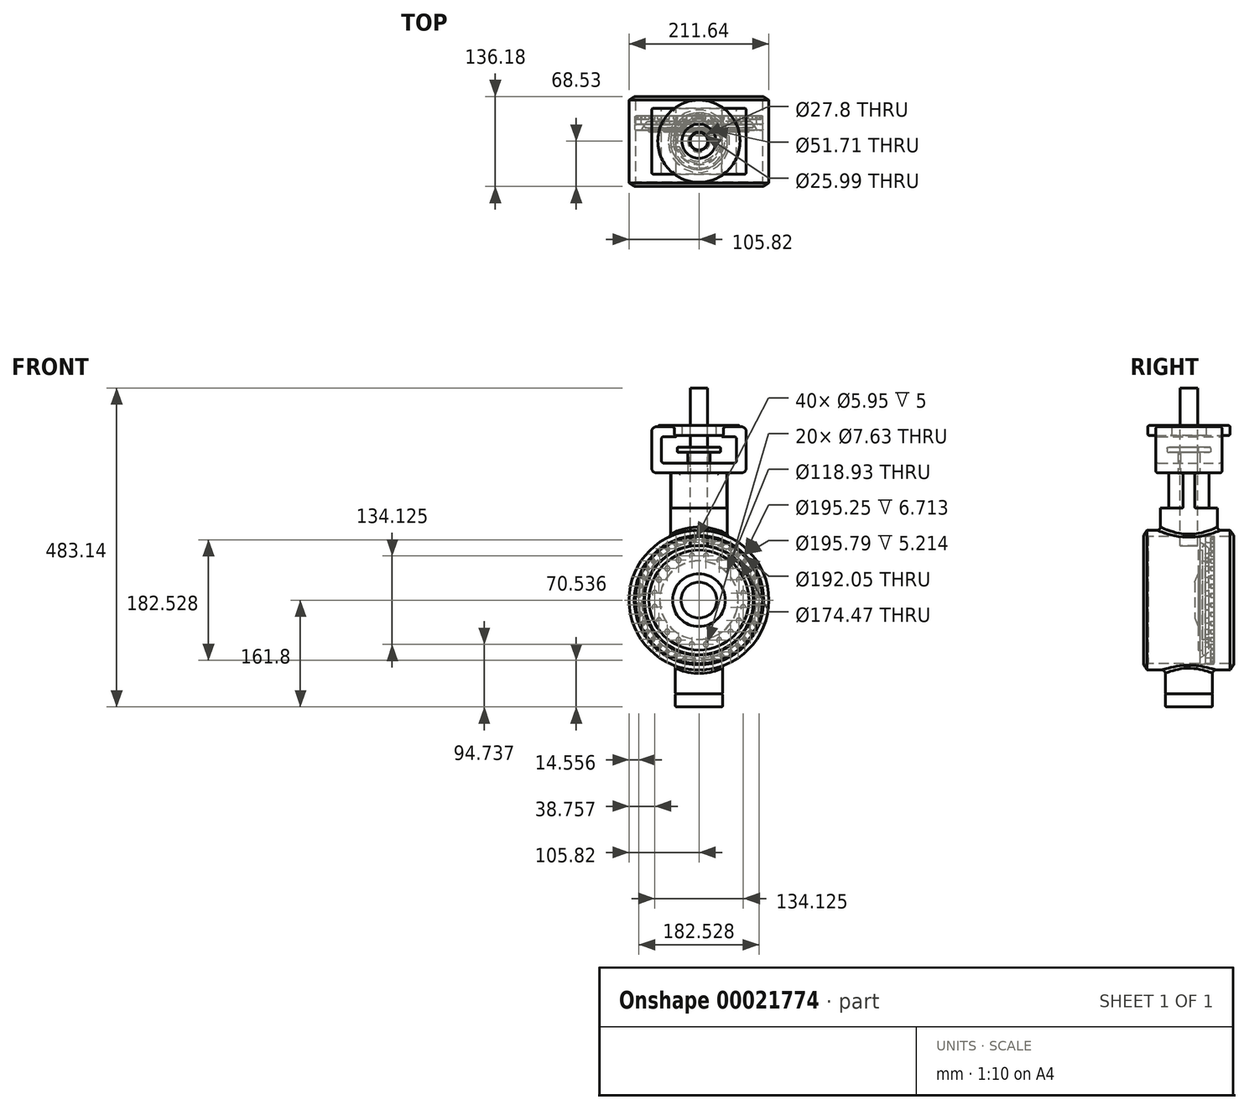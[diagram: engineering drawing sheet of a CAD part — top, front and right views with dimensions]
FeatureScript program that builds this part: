
annotation { "Feature Type Name" : "Feature", "Feature Type Description" : "" }
export const myFeature = defineFeature(function(context is Context, id is Id, definition is map)
    precondition{}
    {
        {
            var Q0;
            Q0=qCreatedBy(makeId("Right.planeOp"),FACE);
            var sketch = newSketch(context, id + "F0", { "sketchPlane" : qUnion([Q0])});
            skLineSegment(sketch, "E0", {"start": v(0, 169.32) * mm, "end": v(-43.14, 169.32) * mm});
            skLineSegment(sketch, "E1", {"start": v(-43.14, 169.32) * mm, "end": v(-43.14, 19.29) * mm});
            skLineSegment(sketch, "E2", {"start": v(-43.14, 19.29) * mm, "end": v(0, 19.29) * mm});
            skLineSegment(sketch, "E3", {"start": v(0, 19.29) * mm, "end": v(0, 169.32) * mm});
            skLineSegment(sketch, "E4", {"start": v(0, -141.8) * mm, "end": v(-35.7, -141.8) * mm});
            skLineSegment(sketch, "E5", {"start": v(-35.7, -141.8) * mm, "end": v(-35.7, -21.86) * mm});
            skLineSegment(sketch, "E6", {"start": v(-35.7, -21.86) * mm, "end": v(0, -21.86) * mm});
            skLineSegment(sketch, "E7", {"start": v(0, -21.86) * mm, "end": v(0, -141.8) * mm});
            skSolve(sketch);
        }
        {
            var Q0;
            Q0=makeQuery(id+"F0.imprint","IMPRINT",FACE,{"disambiguationData":[TD([[makeQuery(id+"F0.imprint","IMPRINT",EDGE,{"derivedFrom":sQuery(id+"F0.wireOp",EDGE,"E4")}),-1.0]])]});
            var Q1;
            Q1=makeQuery(id+"F0.imprint","IMPRINT",FACE,{"disambiguationData":[TD([[makeQuery(id+"F0.imprint","IMPRINT",EDGE,{"derivedFrom":sQuery(id+"F0.wireOp",EDGE,"E0")}),1.0]])]});
            var Q2;
            Q2=sQuery(id+"F0.wireOp",EDGE,"E3");
            revolve(context, id + "F1", {"entities" : qUnion([Q0, Q1]), "axis" : qUnion([Q2]), "revolveType" : RevolveType.FULL});
        }
        {
            var Q0;
            Q0=qCreatedBy(makeId("Right.planeOp"),FACE);
            var sketch = newSketch(context, id + "F2", { "sketchPlane" : qUnion([Q0])});
            skLineSegment(sketch, "E8", {"start": v(-63.23, 105.82) * mm, "end": v(-68.53, 97.88) * mm});
            skLineSegment(sketch, "E9", {"start": v(-68.53, 97.88) * mm, "end": v(-68.53, 0) * mm});
            skLineSegment(sketch, "E10", {"start": v(-68.53, 0) * mm, "end": v(67.92, 0) * mm});
            skLineSegment(sketch, "E11", {"start": v(67.92, 0) * mm, "end": v(67.92, 97.48) * mm});
            skLineSegment(sketch, "E12", {"start": v(67.92, 97.48) * mm, "end": v(62.47, 105.82) * mm});
            skLineSegment(sketch, "E13", {"start": v(62.47, 105.82) * mm, "end": v(-63.23, 105.82) * mm});
            skSolve(sketch);
        }
        {
            var Q0;
            Q0 = qSketchRegion(id + "F2", true);
            var Q1;
            Q1=sQuery(id+"F2.wireOp",EDGE,"E10");
            revolve(context, id + "F3", {"operationType" : NewBodyOperationType.ADD, "entities" : qUnion([Q0]), "axis" : qUnion([Q1]), "revolveType" : RevolveType.FULL});
        }
        {
            var Q0;
            Q0=qCreatedBy(makeId("Right.planeOp"),FACE);
            var sketch = newSketch(context, id + "F4", { "sketchPlane" : qUnion([Q0])});
            skLineSegment(sketch, "E14", {"start": v(75.61, 0) * mm, "end": v(-75.09, 0) * mm});
            skLineSegment(sketch, "E15", {"start": v(-75.09, 0) * mm, "end": v(-75.09, 97.63) * mm});
            skLineSegment(sketch, "E16", {"start": v(-75.09, 97.63) * mm, "end": v(-61.81, 97.63) * mm});
            skLineSegment(sketch, "E17", {"start": v(-61.81, 97.63) * mm, "end": v(-61.81, 96.02) * mm});
            skLineSegment(sketch, "E18", {"start": v(-61.81, 96.02) * mm, "end": v(62.44, 96.02) * mm});
            skLineSegment(sketch, "E19", {"start": v(62.44, 96.02) * mm, "end": v(62.44, 97.9) * mm});
            skLineSegment(sketch, "E20", {"start": v(62.44, 97.9) * mm, "end": v(75.61, 97.9) * mm});
            skLineSegment(sketch, "E21", {"start": v(75.61, 97.9) * mm, "end": v(75.61, 0) * mm});
            skSolve(sketch);
        }
        {
            var Q0;
            Q0 = qSketchRegion(id + "F4", true);
            var Q1;
            Q1=sQuery(id+"F4.wireOp",EDGE,"E14");
            revolve(context, id + "F5", {"operationType" : NewBodyOperationType.REMOVE, "entities" : qUnion([Q0]), "axis" : qUnion([Q1]), "revolveType" : RevolveType.FULL, "oppositeDirection" : true});
        }
        {
            var Q0;
            Q0=qCreatedBy(makeId("Right.planeOp"),FACE);
            var sketch = newSketch(context, id + "F6", { "sketchPlane" : qUnion([Q0])});
            skLineSegment(sketch, "E22", {"start": v(38.22, -87.24) * mm, "end": v(38.22, -97.03) * mm});
            skLineSegment(sketch, "E23", {"start": v(38.22, -97.03) * mm, "end": v(25.34, -97.03) * mm});
            skLineSegment(sketch, "E24", {"start": v(25.34, -97.03) * mm, "end": v(25.34, -87.24) * mm});
            skLineSegment(sketch, "E25", {"start": v(25.34, -87.24) * mm, "end": v(38.22, -87.24) * mm});
            skSolve(sketch);
        }
        {
            var Q0;
            Q0 = qSketchRegion(id + "F6", true);
            var Q1;
            Q1=makeQuery(id+"F3.opRevolve","SWEPT_FACE",FACE,{"disambiguationData":[OSD([sQuery(id+"F2.wireOp",EDGE,"E13")])]});
            revolve(context, id + "F7", {"entities" : qUnion([Q0]), "axis" : qUnion([Q1]), "revolveType" : RevolveType.FULL});
        }
        {
            var Q0;
            Q0=qCreatedBy(makeId("Right.planeOp"),FACE);
            var sketch = newSketch(context, id + "F8", { "sketchPlane" : qUnion([Q0])});
            skLineSegment(sketch, "E26", {"start": v(25.46, -96.97) * mm, "end": v(25.46, -82.81) * mm});
            skLineSegment(sketch, "E27", {"start": v(25.46, -82.81) * mm, "end": v(16.75, -87.53) * mm});
            skLineSegment(sketch, "E28", {"start": v(16.75, -87.53) * mm, "end": v(16.75, -96.97) * mm});
            skLineSegment(sketch, "E29", {"start": v(16.75, -96.97) * mm, "end": v(25.46, -96.97) * mm});
            skSolve(sketch);
        }
        {
            var Q0;
            Q0 = qSketchRegion(id + "F8", true);
            var Q1;
            Q1=makeQuery(id+"F3.opRevolve","SWEPT_EDGE",EDGE,{"disambiguationData":[OSD([sQuery(id+"F2.wireOp",EDGE,"E12"),sQuery(id+"F2.wireOp",EDGE,"E13")])]});
            revolve(context, id + "F9", {"entities" : qUnion([Q0]), "axis" : qUnion([Q1]), "revolveType" : RevolveType.FULL});
        }
        {
            var Q0;
            Q0=qCreatedBy(makeId("Right.planeOp"),FACE);
            var sketch = newSketch(context, id + "F10", { "sketchPlane" : qUnion([Q0])});
            skLineSegment(sketch, "E30", {"start": v(29.76, -59.47) * mm, "end": v(29.76, -78.81) * mm});
            skLineSegment(sketch, "E31", {"start": v(29.76, -78.81) * mm, "end": v(25.48, -82.48) * mm});
            skLineSegment(sketch, "E32", {"start": v(25.48, -82.48) * mm, "end": v(20.8, -82.48) * mm});
            skLineSegment(sketch, "E33", {"start": v(20.8, -82.48) * mm, "end": v(20.8, -59.47) * mm});
            skLineSegment(sketch, "E34", {"start": v(20.8, -59.47) * mm, "end": v(29.76, -59.47) * mm});
            skSolve(sketch);
        }
        {
            var Q0;
            Q0 = qSketchRegion(id + "F10", true);
            var Q1;
            Q1=makeQuery(id+"F3.opRevolve","SWEPT_EDGE",EDGE,{"disambiguationData":[OSD([sQuery(id+"F2.wireOp",EDGE,"E12"),sQuery(id+"F2.wireOp",EDGE,"E13")])]});
            revolve(context, id + "F11", {"entities" : qUnion([Q0]), "axis" : qUnion([Q1]), "revolveType" : RevolveType.FULL});
        }
        {
            var Q0;
            Q0=qCreatedBy(makeId("Right.planeOp"),FACE);
            var sketch = newSketch(context, id + "F12", { "sketchPlane" : qUnion([Q0])});
            skLineSegment(sketch, "E35", {"start": v(24.9, -59.2) * mm, "end": v(24.9, 0) * mm});
            skLineSegment(sketch, "E36", {"start": v(24.9, 0) * mm, "end": v(8.58, 0) * mm});
            skLineSegment(sketch, "E37", {"start": v(8.58, 0) * mm, "end": v(8.58, -27.12) * mm});
            skLineSegment(sketch, "E38", {"start": v(8.58, -27.12) * mm, "end": v(14.02, -39.9) * mm});
            skLineSegment(sketch, "E39", {"start": v(14.02, -39.9) * mm, "end": v(14.02, -75.69) * mm});
            skLineSegment(sketch, "E40", {"start": v(14.02, -75.69) * mm, "end": v(20.07, -75.69) * mm});
            skLineSegment(sketch, "E41", {"start": v(20.07, -75.69) * mm, "end": v(20.07, -59.2) * mm});
            skLineSegment(sketch, "E42", {"start": v(20.07, -59.2) * mm, "end": v(24.9, -59.2) * mm});
            skSolve(sketch);
        }
        {
            var Q0;
            Q0 = qSketchRegion(id + "F12", true);
            var Q1;
            Q1=sQuery(id+"F12.wireOp",EDGE,"E36");
            revolve(context, id + "F13", {"entities" : qUnion([Q0]), "axis" : qUnion([Q1]), "revolveType" : RevolveType.FULL});
        }
        {
            var Q0;
            Q0=makeQuery(id+"F11.opRevolve","SWEPT_FACE",FACE,{"disambiguationData":[OSD([sQuery(id+"F10.wireOp",EDGE,"E30")])]});
            var sketch = newSketch(context, id + "F14", { "sketchPlane" : qUnion([Q0])});
            skLineSegment(sketch, "E43", {"start": v(0, 0) * mm, "end": v(12.55, 79.96) * mm, "construction": true});
            skCircle(sketch, "E44", {"center": v(10.53, 67.06) * mm, "radius": 3.81 * mm});
            skSolve(sketch);
        }
        {
            var Q0;
            Q0 = qSketchRegion(id + "F14", true);
            extrude(context, id + "F15", {"entities" : qUnion([Q0]), "oppositeDirection" : true, "depth" : 5 * mm});
        }
        {
            var Q0;
            Q0=makeQuery(id+"F15.opExtrude","SWEPT_BODY",BODY,{"disambiguationData":[OSD([sQuery(id+"F14.wireOp",EDGE,"E44")])]});
            var Q1;
            Q1=makeQuery(id+"F11.opRevolve","SWEPT_EDGE",EDGE,{"disambiguationData":[OSD([sQuery(id+"F10.wireOp",EDGE,"E30"),sQuery(id+"F10.wireOp",EDGE,"E34")])]});
            circularPattern(context, id + "F16", {"operationType" : NewBodyOperationType.REMOVE, "entities" : qUnion([Q0]), "axis" : qUnion([Q1]), "angle" : 360 * degree, "instanceCount" : 20, "equalSpace" : true});
        }
        {
            var Q0;
            Q0=makeQuery(id+"F7.opRevolve","SWEPT_FACE",FACE,{"disambiguationData":[OSD([sQuery(id+"F6.wireOp",EDGE,"E22")])]});
            var sketch = newSketch(context, id + "F17", { "sketchPlane" : qUnion([Q0])});
            skLineSegment(sketch, "E45", {"start": v(0, 0) * mm, "end": v(8.01, 104.27) * mm, "construction": true});
            skCircle(sketch, "E46", {"center": v(7.01, 91.26) * mm, "radius": 2.97 * mm});
            skSolve(sketch);
        }
        {
            var Q0;
            Q0 = qSketchRegion(id + "F17", true);
            extrude(context, id + "F18", {"entities" : qUnion([Q0]), "oppositeDirection" : true, "depth" : 5 * mm});
        }
        {
            var Q0;
            Q0=makeQuery(id+"F18.opExtrude","SWEPT_BODY",BODY,{"disambiguationData":[OSD([sQuery(id+"F17.wireOp",EDGE,"E46")])]});
            var Q1;
            Q1=makeQuery(id+"F7.opRevolve","SWEPT_EDGE",EDGE,{"disambiguationData":[OSD([sQuery(id+"F6.wireOp",EDGE,"E22"),sQuery(id+"F6.wireOp",EDGE,"E25")])]});
            circularPattern(context, id + "F19", {"operationType" : NewBodyOperationType.REMOVE, "entities" : qUnion([Q0]), "axis" : qUnion([Q1]), "angle" : 360 * degree, "instanceCount" : 40, "equalSpace" : true});
        }
        {
            var Q0;
            Q0=makeQuery(id+"F1.opRevolve","SWEPT_FACE",FACE,{"disambiguationData":[OSD([sQuery(id+"F0.wireOp",EDGE,"E4")])]});
            extrude(context, id + "F20", {"entities" : qUnion([Q0]), "depth" : 20 * mm});
        }
        {
            var Q0;
            Q0=makeQuery(id+"F1.opRevolve","SWEPT_FACE",FACE,{"disambiguationData":[OSD([sQuery(id+"F0.wireOp",EDGE,"E0")])]});
            var sketch = newSketch(context, id + "F21", { "sketchPlane" : qUnion([Q0])});
            skArc(sketch, "E47", {"start": v(28.97, 8.71) * mm, "mid": v(0, 30.25) * mm, "end": v(-28.97, 8.71) * mm});
            skLineSegment(sketch, "E48", {"start": v(28.97, -8.71) * mm, "end": v(42.25, -8.71) * mm});
            skArc(sketch, "E49.0", {"start": v(-42.25, -8.71) * mm, "mid": v(0, -43.14) * mm, "end": v(42.25, -8.71) * mm});
            skLineSegment(sketch, "E50", {"start": v(0, -43.14) * mm, "end": v(0, 43.14) * mm, "construction": true});
            skLineSegment(sketch, "E51", {"start": v(43.14, 0) * mm, "end": v(-43.14, 0) * mm, "construction": true});
            skLineSegment(sketch, "E52.MirrorCS", {"start": v(28.97, 8.71) * mm, "end": v(42.25, 8.71) * mm});
            skLineSegment(sketch, "E53.MirrorCS", {"start": v(-28.97, -8.71) * mm, "end": v(-42.25, -8.71) * mm});
            skLineSegment(sketch, "E54.MirrorCS", {"start": v(-28.97, 8.71) * mm, "end": v(-42.25, 8.71) * mm});
            skArc(sketch, "E55.trimOffspring", {"start": v(-28.97, -8.71) * mm, "mid": v(0, -30.25) * mm, "end": v(28.97, -8.71) * mm});
            skArc(sketch, "E56.trimOffspring", {"start": v(42.25, 8.71) * mm, "mid": v(0, 43.14) * mm, "end": v(-42.25, 8.71) * mm});
            skSolve(sketch);
        }
        {
            var Q0;
            Q0 = qSketchRegion(id + "F21", true);
            extrude(context, id + "F22", {"entities" : qUnion([Q0]), "operationType" : NewBodyOperationType.REMOVE, "oppositeDirection" : true, "depth" : 30 * mm});
        }
        {
            var Q0;
            Q0=makeQuery(id+"F1.opRevolve","SWEPT_FACE",FACE,{"disambiguationData":[OSD([sQuery(id+"F0.wireOp",EDGE,"E0")])]});
            extrude(context, id + "F23", {"entities" : qUnion([Q0]), "operationType" : NewBodyOperationType.ADD, "depth" : 25 * mm});
        }
        {
            var Q0;
            Q0=qCreatedBy(makeId("Front.planeOp"),FACE);
            var sketch = newSketch(context, id + "F24", { "sketchPlane" : qUnion([Q0])});
            skLineSegment(sketch, "E57", {"start": v(0, 192.64) * mm, "end": v(-71.67, 192.64) * mm});
            skLineSegment(sketch, "E58", {"start": v(-71.67, 192.64) * mm, "end": v(-71.67, 262.55) * mm});
            skLineSegment(sketch, "E59", {"start": v(-71.67, 262.55) * mm, "end": v(-34.47, 262.55) * mm});
            skLineSegment(sketch, "E60", {"start": v(-34.47, 262.55) * mm, "end": v(-34.47, 247.55) * mm});
            skLineSegment(sketch, "E61", {"start": v(-34.47, 247.55) * mm, "end": v(-56.67, 247.55) * mm});
            skLineSegment(sketch, "E62", {"start": v(-56.67, 247.55) * mm, "end": v(-56.67, 207.64) * mm});
            skLineSegment(sketch, "E63", {"start": v(-56.67, 207.64) * mm, "end": v(0, 207.64) * mm});
            skLineSegment(sketch, "E64", {"start": v(0, 207.64) * mm, "end": v(0, 192.64) * mm});
            skSolve(sketch);
        }
        {
            var Q0;
            Q0 = qSketchRegion(id + "F24", true);
            extrude(context, id + "F25", {"entities" : qUnion([Q0]), "endBound" : BoundingType.SYMMETRIC, "depth" : 100 * mm});
        }
        {
            var Q0;
            Q0=makeQuery(id+"F25.opExtrude","SWEPT_BODY",BODY,{"disambiguationData":[OSD([sQuery(id+"F24.wireOp",EDGE,"E57"),sQuery(id+"F24.wireOp",EDGE,"E58"),sQuery(id+"F24.wireOp",EDGE,"E59"),sQuery(id+"F24.wireOp",EDGE,"E60"),sQuery(id+"F24.wireOp",EDGE,"E61"),sQuery(id+"F24.wireOp",EDGE,"E62"),sQuery(id+"F24.wireOp",EDGE,"E63"),sQuery(id+"F24.wireOp",EDGE,"E64")])]});
            var Q1;
            Q1=makeQuery(id+"F25.opExtrude","SWEPT_FACE",FACE,{"disambiguationData":[OSD([sQuery(id+"F24.wireOp",EDGE,"E64")])]});
            mirror(context, id + "F26", {"operationType" : NewBodyOperationType.ADD, "entities" : qUnion([Q0]), "mirrorPlane" : qUnion([Q1])});
        }
        {
            var Q0;
            Q0=makeQuery(id+"F26.opPattern","COPY",EDGE,{"derivedFrom":makeQuery(id+"F25.opExtrude","SWEPT_EDGE",EDGE,{"disambiguationData":[OSD([sQuery(id+"F24.wireOp",EDGE,"E57"),sQuery(id+"F24.wireOp",EDGE,"E58")])]}),"instanceName":"1"});
            var Q1;
            Q1=makeQuery(id+"F25.opExtrude","SWEPT_EDGE",EDGE,{"disambiguationData":[OSD([sQuery(id+"F24.wireOp",EDGE,"E57"),sQuery(id+"F24.wireOp",EDGE,"E58")])]});
            var Q2;
            Q2=makeQuery(id+"F26.opPattern","COPY",EDGE,{"derivedFrom":makeQuery(id+"F25.opExtrude","SWEPT_EDGE",EDGE,{"disambiguationData":[OSD([sQuery(id+"F24.wireOp",EDGE,"E58"),sQuery(id+"F24.wireOp",EDGE,"E59")])]}),"instanceName":"1"});
            var Q3;
            Q3=makeQuery(id+"F25.opExtrude","SWEPT_EDGE",EDGE,{"disambiguationData":[OSD([sQuery(id+"F24.wireOp",EDGE,"E58"),sQuery(id+"F24.wireOp",EDGE,"E59")])]});
            fillet(context, id + "F27", {"entities" : qUnion([Q0, Q1, Q2, Q3]), "radius" : 7.5 * mm, "tangentPropagation" : true, "allowEdgeOverflow" : false});
        }
        {
            var Q0;
            Q0=makeQuery(id+"F26.opPattern","COPY",EDGE,{"derivedFrom":makeQuery(id+"F25.opExtrude","SWEPT_EDGE",EDGE,{"disambiguationData":[OSD([sQuery(id+"F24.wireOp",EDGE,"E62"),sQuery(id+"F24.wireOp",EDGE,"E63")])]}),"instanceName":"1"});
            var Q1;
            Q1=makeQuery(id+"F26.opPattern","COPY",EDGE,{"derivedFrom":makeQuery(id+"F25.opExtrude","SWEPT_EDGE",EDGE,{"disambiguationData":[OSD([sQuery(id+"F24.wireOp",EDGE,"E61"),sQuery(id+"F24.wireOp",EDGE,"E62")])]}),"instanceName":"1"});
            var Q2;
            Q2=makeQuery(id+"F25.opExtrude","SWEPT_EDGE",EDGE,{"disambiguationData":[OSD([sQuery(id+"F24.wireOp",EDGE,"E61"),sQuery(id+"F24.wireOp",EDGE,"E62")])]});
            var Q3;
            Q3=makeQuery(id+"F25.opExtrude","SWEPT_EDGE",EDGE,{"disambiguationData":[OSD([sQuery(id+"F24.wireOp",EDGE,"E62"),sQuery(id+"F24.wireOp",EDGE,"E63")])]});
            fillet(context, id + "F28", {"entities" : qUnion([Q0, Q1, Q2, Q3]), "radius" : 3.25 * mm, "tangentPropagation" : true, "allowEdgeOverflow" : false});
        }
        {
            var Q0;
            Q0=qCreatedBy(makeId("Right.planeOp"),FACE);
            var sketch = newSketch(context, id + "F29", { "sketchPlane" : qUnion([Q0])});
            skLineSegment(sketch, "E65.bottom", {"start": v(0, 321.34) * mm, "end": v(13.25, 321.34) * mm});
            skLineSegment(sketch, "E65.top", {"start": v(0, 82.11) * mm, "end": v(13.25, 82.11) * mm});
            skLineSegment(sketch, "E65.left", {"start": v(0, 321.34) * mm, "end": v(0, 82.11) * mm});
            skLineSegment(sketch, "E65.right", {"start": v(13.25, 321.34) * mm, "end": v(13.25, 82.11) * mm});
            skSolve(sketch);
        }
        {
            var Q0;
            Q0 = qSketchRegion(id + "F29", true);
            var Q1;
            Q1=sQuery(id+"F29.wireOp",EDGE,"E65.left");
            revolve(context, id + "F30", {"entities" : qUnion([Q0]), "axis" : qUnion([Q1]), "revolveType" : RevolveType.FULL});
        }
        {
            var Q0;
            Q0=qCreatedBy(makeId("Right.planeOp"),FACE);
            var sketch = newSketch(context, id + "F31", { "sketchPlane" : qUnion([Q0])});
            skLineSegment(sketch, "E66.bottom", {"start": v(25.85, 264.26) * mm, "end": v(62.28, 264.26) * mm});
            skLineSegment(sketch, "E66.top", {"start": v(25.85, 249.48) * mm, "end": v(62.28, 249.48) * mm});
            skLineSegment(sketch, "E66.left", {"start": v(25.85, 264.26) * mm, "end": v(25.85, 249.48) * mm});
            skLineSegment(sketch, "E66.right", {"start": v(62.28, 264.26) * mm, "end": v(62.28, 249.48) * mm});
            skSolve(sketch);
        }
        {
            var Q0;
            Q0 = qSketchRegion(id + "F31", true);
            var Q1;
            Q1=makeQuery(id+"F30.opRevolve","SWEPT_FACE",FACE,{"disambiguationData":[OSD([sQuery(id+"F29.wireOp",EDGE,"E65.right")])]});
            revolve(context, id + "F32", {"operationType" : NewBodyOperationType.ADD, "entities" : qUnion([Q0]), "axis" : qUnion([Q1]), "revolveType" : RevolveType.FULL});
        }
        {
            var Q0;
            Q0=qCreatedBy(makeId("Right.planeOp"),FACE);
            var sketch = newSketch(context, id + "F33", { "sketchPlane" : qUnion([Q0])});
            skLineSegment(sketch, "E67.bottom", {"start": v(-13.9, 231.63) * mm, "end": v(-32.97, 231.63) * mm});
            skLineSegment(sketch, "E67.top", {"start": v(-13.9, 223.87) * mm, "end": v(-32.97, 223.87) * mm});
            skLineSegment(sketch, "E67.left", {"start": v(-13.9, 231.63) * mm, "end": v(-13.9, 223.87) * mm});
            skLineSegment(sketch, "E67.right", {"start": v(-32.97, 231.63) * mm, "end": v(-32.97, 223.87) * mm});
            skSolve(sketch);
        }
        {
            var Q0;
            Q0 = qSketchRegion(id + "F33", true);
            var Q1;
            Q1=makeQuery(id+"F30.opRevolve","SWEPT_FACE",FACE,{"disambiguationData":[OSD([sQuery(id+"F29.wireOp",EDGE,"E65.right")])]});
            revolve(context, id + "F34", {"entities" : qUnion([Q0]), "axis" : qUnion([Q1]), "revolveType" : RevolveType.FULL});
        }
        {
            var Q0;
            Q0=qCreatedBy(makeId("Right.planeOp"),FACE);
            var sketch = newSketch(context, id + "F35", { "sketchPlane" : qUnion([Q0])});
            skLineSegment(sketch, "E68.0", {"start": v(32.97, 223.87) * mm, "end": v(-32.97, 223.87) * mm, "construction": true});
            skLineSegment(sketch, "E69.bottom", {"start": v(16.74, 223.87) * mm, "end": v(13, 223.87) * mm});
            skLineSegment(sketch, "E69.top", {"start": v(16.74, 191.56) * mm, "end": v(13, 191.56) * mm});
            skLineSegment(sketch, "E69.left", {"start": v(16.74, 223.87) * mm, "end": v(16.74, 191.56) * mm});
            skLineSegment(sketch, "E69.right", {"start": v(13, 223.87) * mm, "end": v(13, 191.56) * mm});
            skSolve(sketch);
        }
        {
            var Q0;
            Q0 = qSketchRegion(id + "F35", true);
            var Q1;
            Q1=makeQuery(id+"F30.opRevolve","SWEPT_FACE",FACE,{"disambiguationData":[OSD([sQuery(id+"F29.wireOp",EDGE,"E65.right")])]});
            revolve(context, id + "F36", {"entities" : qUnion([Q0]), "axis" : qUnion([Q1]), "revolveType" : RevolveType.FULL});
        }
        {
            var Q0;
            Q0=makeQuery(id+"F3.boolean.opBoolean","INTERSECT",EDGE,{"derivedFrom":[makeQuery(id+"F1.opRevolve","SWEPT_FACE",FACE,{"disambiguationData":[OSD([sQuery(id+"F0.wireOp",EDGE,"E1")])]}),makeQuery(id+"F3.opRevolve","SWEPT_FACE",FACE,{"disambiguationData":[OSD([sQuery(id+"F2.wireOp",EDGE,"E13")])]})]});
            var Q1;
            Q1=makeQuery(id+"F3.boolean.opBoolean","INTERSECT",EDGE,{"derivedFrom":[makeQuery(id+"F1.opRevolve","SWEPT_FACE",FACE,{"disambiguationData":[OSD([sQuery(id+"F0.wireOp",EDGE,"E5")])]}),makeQuery(id+"F3.opRevolve","SWEPT_FACE",FACE,{"disambiguationData":[OSD([sQuery(id+"F2.wireOp",EDGE,"E13")])]})]});
            fillet(context, id + "F37", {"entities" : qUnion([Q0, Q1]), "radius" : 5 * mm, "tangentPropagation" : true, "allowEdgeOverflow" : false});
        }
        {
            var Q0;
            Q0=makeQuery(id+"F22.boolean.opBoolean","COPY",EDGE,{"derivedFrom":makeQuery(id+"F22.opExtrude","CAP_EDGE",EDGE,{"disambiguationData":[OSD([sQuery(id+"F21.wireOp",EDGE,"E47")])],"isStart":false})});
            var Q1;
            Q1=makeQuery(id+"F22.boolean.opBoolean","COPY",EDGE,{"derivedFrom":makeQuery(id+"F22.opExtrude","CAP_EDGE",EDGE,{"disambiguationData":[OSD([sQuery(id+"F21.wireOp",EDGE,"E52.MirrorCS")])],"isStart":false})});
            var Q2;
            Q2=makeQuery(id+"F22.boolean.opBoolean","COPY",EDGE,{"derivedFrom":makeQuery(id+"F22.opExtrude","CAP_EDGE",EDGE,{"disambiguationData":[OSD([sQuery(id+"F21.wireOp",EDGE,"E54.MirrorCS")])],"isStart":false})});
            var Q3;
            Q3=makeQuery(id+"F22.boolean.opBoolean","COPY",EDGE,{"derivedFrom":makeQuery(id+"F22.opExtrude","CAP_EDGE",EDGE,{"disambiguationData":[OSD([sQuery(id+"F21.wireOp",EDGE,"E53.MirrorCS")])],"isStart":false})});
            var Q4;
            Q4=makeQuery(id+"F22.boolean.opBoolean","COPY",EDGE,{"derivedFrom":makeQuery(id+"F22.opExtrude","CAP_EDGE",EDGE,{"disambiguationData":[OSD([sQuery(id+"F21.wireOp",EDGE,"E55.trimOffspring")])],"isStart":false})});
            var Q5;
            Q5=makeQuery(id+"F22.boolean.opBoolean","COPY",EDGE,{"derivedFrom":makeQuery(id+"F22.opExtrude","CAP_EDGE",EDGE,{"disambiguationData":[OSD([sQuery(id+"F21.wireOp",EDGE,"E48")])],"isStart":false})});
            var Q6;
            Q6=makeQuery(id+"F22.boolean.opBoolean","COPY",EDGE,{"derivedFrom":makeQuery(id+"F22.opExtrude","CAP_EDGE",EDGE,{"disambiguationData":[OSD([sQuery(id+"F21.wireOp",EDGE,"E49.0")])],"isStart":false})});
            var Q7;
            Q7=makeQuery(id+"F22.boolean.opBoolean","COPY",EDGE,{"derivedFrom":makeQuery(id+"F22.opExtrude","CAP_EDGE",EDGE,{"disambiguationData":[OSD([sQuery(id+"F21.wireOp",EDGE,"E56.trimOffspring")])],"isStart":false})});
            var Q8;
            {var subQ0=sQuery(id+"F21.wireOp",EDGE,"E47");var subQ1=sQuery(id+"F21.wireOp",EDGE,"E52.MirrorCS");Q8=makeQuery(id+"F23.boolean.opBoolean","MERGE",EDGE,{"derivedFrom":[makeQuery(id+"F22.boolean.opBoolean","COPY",EDGE,{"derivedFrom":makeQuery(id+"F22.opExtrude","SWEPT_EDGE",EDGE,{"disambiguationData":[OSD([subQ0,subQ1])]})}),makeQuery(id+"F23.opExtrude","SWEPT_EDGE",EDGE,{"disambiguationData":[OSD([subQ0,subQ1])]})]});}
            var Q9;
            {var subQ0=sQuery(id+"F21.wireOp",EDGE,"E48");var subQ1=sQuery(id+"F21.wireOp",EDGE,"E55.trimOffspring");Q9=makeQuery(id+"F23.boolean.opBoolean","MERGE",EDGE,{"derivedFrom":[makeQuery(id+"F22.boolean.opBoolean","COPY",EDGE,{"derivedFrom":makeQuery(id+"F22.opExtrude","SWEPT_EDGE",EDGE,{"disambiguationData":[OSD([subQ0,subQ1])]})}),makeQuery(id+"F23.opExtrude","SWEPT_EDGE",EDGE,{"disambiguationData":[OSD([subQ0,subQ1])]})]});}
            var Q10;
            {var subQ0=sQuery(id+"F21.wireOp",EDGE,"E53.MirrorCS");var subQ1=sQuery(id+"F21.wireOp",EDGE,"E55.trimOffspring");Q10=makeQuery(id+"F23.boolean.opBoolean","MERGE",EDGE,{"derivedFrom":[makeQuery(id+"F22.boolean.opBoolean","COPY",EDGE,{"derivedFrom":makeQuery(id+"F22.opExtrude","SWEPT_EDGE",EDGE,{"disambiguationData":[OSD([subQ0,subQ1])]})}),makeQuery(id+"F23.opExtrude","SWEPT_EDGE",EDGE,{"disambiguationData":[OSD([subQ0,subQ1])]})]});}
            var Q11;
            {var subQ0=sQuery(id+"F21.wireOp",EDGE,"E47");var subQ1=sQuery(id+"F21.wireOp",EDGE,"E54.MirrorCS");Q11=makeQuery(id+"F23.boolean.opBoolean","MERGE",EDGE,{"derivedFrom":[makeQuery(id+"F22.boolean.opBoolean","COPY",EDGE,{"derivedFrom":makeQuery(id+"F22.opExtrude","SWEPT_EDGE",EDGE,{"disambiguationData":[OSD([subQ0,subQ1])]})}),makeQuery(id+"F23.opExtrude","SWEPT_EDGE",EDGE,{"disambiguationData":[OSD([subQ0,subQ1])]})]});}
            var Q12;
            {var subQ0=sQuery(id+"F21.wireOp",EDGE,"E54.MirrorCS");var subQ1=makeQuery(id+"F25.opExtrude","SWEPT_FACE",FACE,{"disambiguationData":[OSD([sQuery(id+"F24.wireOp",EDGE,"E57")])]});Q12=makeQuery(id+"F26.boolean.opBoolean","INTERSECT",EDGE,{"derivedFrom":[makeQuery(id+"F23.boolean.opBoolean","MERGE",FACE,{"derivedFrom":[makeQuery(id+"F22.boolean.opBoolean","COPY",FACE,{"derivedFrom":makeQuery(id+"F22.opExtrude","SWEPT_FACE",FACE,{"disambiguationData":[OSD([subQ0])]})}),makeQuery(id+"F23.opExtrude","SWEPT_FACE",FACE,{"disambiguationData":[OSD([subQ0])]})]}),subQ1,makeQuery(id+"F26.opPattern","COPY",FACE,{"derivedFrom":subQ1,"instanceName":"1"})]});}
            var Q13;
            {var subQ0=sQuery(id+"F21.wireOp",EDGE,"E52.MirrorCS");var subQ1=makeQuery(id+"F25.opExtrude","SWEPT_FACE",FACE,{"disambiguationData":[OSD([sQuery(id+"F24.wireOp",EDGE,"E57")])]});Q13=makeQuery(id+"F26.boolean.opBoolean","INTERSECT",EDGE,{"derivedFrom":[makeQuery(id+"F23.boolean.opBoolean","MERGE",FACE,{"derivedFrom":[makeQuery(id+"F22.boolean.opBoolean","COPY",FACE,{"derivedFrom":makeQuery(id+"F22.opExtrude","SWEPT_FACE",FACE,{"disambiguationData":[OSD([subQ0])]})}),makeQuery(id+"F23.opExtrude","SWEPT_FACE",FACE,{"disambiguationData":[OSD([subQ0])]})]}),subQ1,makeQuery(id+"F26.opPattern","COPY",FACE,{"derivedFrom":subQ1,"instanceName":"1"})]});}
            var Q14;
            {var subQ0=sQuery(id+"F21.wireOp",EDGE,"E47");var subQ1=makeQuery(id+"F25.opExtrude","SWEPT_FACE",FACE,{"disambiguationData":[OSD([sQuery(id+"F24.wireOp",EDGE,"E57")])]});Q14=makeQuery(id+"F26.boolean.opBoolean","INTERSECT",EDGE,{"derivedFrom":[makeQuery(id+"F23.boolean.opBoolean","MERGE",FACE,{"derivedFrom":[makeQuery(id+"F22.boolean.opBoolean","COPY",FACE,{"derivedFrom":makeQuery(id+"F22.opExtrude","SWEPT_FACE",FACE,{"disambiguationData":[OSD([subQ0])]})}),makeQuery(id+"F23.opExtrude","SWEPT_FACE",FACE,{"disambiguationData":[OSD([subQ0])]})]}),subQ1,makeQuery(id+"F26.opPattern","COPY",FACE,{"derivedFrom":subQ1,"instanceName":"1"})]});}
            var Q15;
            {var subQ0=sQuery(id+"F21.wireOp",EDGE,"E55.trimOffspring");var subQ1=makeQuery(id+"F25.opExtrude","SWEPT_FACE",FACE,{"disambiguationData":[OSD([sQuery(id+"F24.wireOp",EDGE,"E57")])]});Q15=makeQuery(id+"F26.boolean.opBoolean","INTERSECT",EDGE,{"derivedFrom":[makeQuery(id+"F23.boolean.opBoolean","MERGE",FACE,{"derivedFrom":[makeQuery(id+"F22.boolean.opBoolean","COPY",FACE,{"derivedFrom":makeQuery(id+"F22.opExtrude","SWEPT_FACE",FACE,{"disambiguationData":[OSD([subQ0])]})}),makeQuery(id+"F23.opExtrude","SWEPT_FACE",FACE,{"disambiguationData":[OSD([subQ0])]})]}),subQ1,makeQuery(id+"F26.opPattern","COPY",FACE,{"derivedFrom":subQ1,"instanceName":"1"})]});}
            fillet(context, id + "F38", {"entities" : qUnion([Q0, Q1, Q2, Q3, Q4, Q5, Q6, Q7, Q8, Q9, Q10, Q11, Q12, Q13, Q14, Q15]), "radius" : 2 * mm, "tangentPropagation" : true, "allowEdgeOverflow" : false});
        }
        {
            var Q0;
            Q0=makeQuery(id+"F25.opExtrude","CAP_EDGE",EDGE,{"disambiguationData":[OSD([sQuery(id+"F24.wireOp",EDGE,"E58")])],"isStart":false});
            var Q1;
            Q1=makeQuery(id+"F25.opExtrude","CAP_EDGE",EDGE,{"disambiguationData":[OSD([sQuery(id+"F24.wireOp",EDGE,"E62")])],"isStart":false});
            var Q2;
            Q2=makeQuery(id+"F25.opExtrude","CAP_EDGE",EDGE,{"disambiguationData":[OSD([sQuery(id+"F24.wireOp",EDGE,"E62")])],"isStart":true});
            var Q3;
            Q3=makeQuery(id+"F25.opExtrude","CAP_EDGE",EDGE,{"disambiguationData":[OSD([sQuery(id+"F24.wireOp",EDGE,"E58")])],"isStart":true});
            fillet(context, id + "F39", {"entities" : qUnion([Q0, Q1, Q2, Q3]), "radius" : 3 * mm, "tangentPropagation" : true, "allowEdgeOverflow" : false});
        }
        {
            var Q0;
            Q0=makeQuery(id+"F32.opRevolve","SWEPT_EDGE",EDGE,{"disambiguationData":[OSD([sQuery(id+"F31.wireOp",EDGE,"E66.bottom"),sQuery(id+"F31.wireOp",EDGE,"E66.right")])]});
            var Q1;
            Q1=makeQuery(id+"F32.opRevolve","SWEPT_FACE",FACE,{"disambiguationData":[OSD([sQuery(id+"F31.wireOp",EDGE,"E66.left")])]});
            var Q2;
            {var subQ0=sQuery(id+"F31.wireOp",EDGE,"E66.top");var subQ1=sQuery(id+"F31.wireOp",EDGE,"E66.right");var subQ2=makeQuery(id+"F25.opExtrude","CAP_FACE",FACE,{"disambiguationData":[OSD([sQuery(id+"F24.wireOp",EDGE,"E57"),sQuery(id+"F24.wireOp",EDGE,"E58"),sQuery(id+"F24.wireOp",EDGE,"E59"),sQuery(id+"F24.wireOp",EDGE,"E60"),sQuery(id+"F24.wireOp",EDGE,"E61"),sQuery(id+"F24.wireOp",EDGE,"E62"),sQuery(id+"F24.wireOp",EDGE,"E63"),sQuery(id+"F24.wireOp",EDGE,"E64")])],"isStart":false});Q2=makeQuery(id+"F32.boolean.opBoolean","SPLIT",EDGE,{"disambiguationData":[TD([subQ2])],"derivedFrom":makeQuery(id+"F32.opRevolve","SWEPT_EDGE",EDGE,{"disambiguationData":[OSD([subQ0,subQ1])]})});}
            var Q3;
            {var subQ0=sQuery(id+"F31.wireOp",EDGE,"E66.top");var subQ1=sQuery(id+"F31.wireOp",EDGE,"E66.right");var subQ2=makeQuery(id+"F25.opExtrude","CAP_FACE",FACE,{"disambiguationData":[OSD([sQuery(id+"F24.wireOp",EDGE,"E57"),sQuery(id+"F24.wireOp",EDGE,"E58"),sQuery(id+"F24.wireOp",EDGE,"E59"),sQuery(id+"F24.wireOp",EDGE,"E60"),sQuery(id+"F24.wireOp",EDGE,"E61"),sQuery(id+"F24.wireOp",EDGE,"E62"),sQuery(id+"F24.wireOp",EDGE,"E63"),sQuery(id+"F24.wireOp",EDGE,"E64")])],"isStart":true});Q3=makeQuery(id+"F32.boolean.opBoolean","SPLIT",EDGE,{"disambiguationData":[TD([subQ2])],"derivedFrom":makeQuery(id+"F32.opRevolve","SWEPT_EDGE",EDGE,{"disambiguationData":[OSD([subQ0,subQ1])]})});}
            fillet(context, id + "F40", {"entities" : qUnion([Q0, Q1, Q2, Q3]), "radius" : 2 * mm, "tangentPropagation" : true, "allowEdgeOverflow" : false});
        }
        {
            var Q0;
            Q0=makeQuery(id+"F1.opRevolve","SWEPT_FACE",FACE,{"disambiguationData":[OSD([sQuery(id+"F0.wireOp",EDGE,"E4")])]});
            fillet(context, id + "F41", {"entities" : qUnion([Q0]), "radius" : 2 * mm, "tangentPropagation" : true, "allowEdgeOverflow" : false});
        }
        {
            var Q0;
            Q0=makeQuery(id+"F5.boolean.opBoolean","COPY",FACE,{"derivedFrom":makeQuery(id+"F5.opRevolve","SWEPT_FACE",FACE,{"disambiguationData":[OSD([sQuery(id+"F4.wireOp",EDGE,"E18")])]})});
            fillet(context, id + "F42", {"entities" : qUnion([Q0]), "radius" : 1 * mm, "tangentPropagation" : true, "allowEdgeOverflow" : false});
        }
        {
            var Q0;
            Q0=makeQuery(id+"F7.opRevolve","SWEPT_FACE",FACE,{"disambiguationData":[OSD([sQuery(id+"F6.wireOp",EDGE,"E25")])]});
            var Q1;
            Q1=makeQuery(id+"F7.opRevolve","SWEPT_FACE",FACE,{"disambiguationData":[OSD([sQuery(id+"F6.wireOp",EDGE,"E23")])]});
            fillet(context, id + "F43", {"entities" : qUnion([Q0, Q1]), "radius" : 2 * mm, "tangentPropagation" : true, "allowEdgeOverflow" : false});
        }
        {
            var Q0;
            Q0=makeQuery(id+"F9.opRevolve","SWEPT_FACE",FACE,{"disambiguationData":[OSD([sQuery(id+"F8.wireOp",EDGE,"E27")])]});
            var Q1;
            Q1=makeQuery(id+"F9.opRevolve","SWEPT_FACE",FACE,{"disambiguationData":[OSD([sQuery(id+"F8.wireOp",EDGE,"E29")])]});
            fillet(context, id + "F44", {"entities" : qUnion([Q0, Q1]), "radius" : 1 * mm, "tangentPropagation" : true, "allowEdgeOverflow" : false});
        }
        {
            var Q0;
            Q0=makeQuery(id+"F11.opRevolve","SWEPT_FACE",FACE,{"disambiguationData":[OSD([sQuery(id+"F10.wireOp",EDGE,"E34")])]});
            var Q1;
            Q1=makeQuery(id+"F11.opRevolve","SWEPT_FACE",FACE,{"disambiguationData":[OSD([sQuery(id+"F10.wireOp",EDGE,"E32")])]});
            var Q2;
            Q2=makeQuery(id+"F11.opRevolve","SWEPT_EDGE",EDGE,{"disambiguationData":[OSD([sQuery(id+"F10.wireOp",EDGE,"E30"),sQuery(id+"F10.wireOp",EDGE,"E31")])]});
            var Q3;
            Q3=makeQuery(id+"F16.boolean.opBoolean","COPY",FACE,{"derivedFrom":makeQuery(id+"F15.opExtrude","SWEPT_FACE",FACE,{"disambiguationData":[OSD([sQuery(id+"F14.wireOp",EDGE,"E44")])]})});
            var Q4;
            Q4=makeQuery(id+"F16.boolean.opBoolean","COPY",FACE,{"derivedFrom":makeQuery(id+"F16.opPattern","COPY",FACE,{"derivedFrom":makeQuery(id+"F15.opExtrude","SWEPT_FACE",FACE,{"disambiguationData":[OSD([sQuery(id+"F14.wireOp",EDGE,"E44")])]}),"instanceName":"1"})});
            var Q5;
            Q5=makeQuery(id+"F16.boolean.opBoolean","COPY",FACE,{"derivedFrom":makeQuery(id+"F16.opPattern","COPY",FACE,{"derivedFrom":makeQuery(id+"F15.opExtrude","SWEPT_FACE",FACE,{"disambiguationData":[OSD([sQuery(id+"F14.wireOp",EDGE,"E44")])]}),"instanceName":"2"})});
            var Q6;
            Q6=makeQuery(id+"F16.boolean.opBoolean","COPY",FACE,{"derivedFrom":makeQuery(id+"F16.opPattern","COPY",FACE,{"derivedFrom":makeQuery(id+"F15.opExtrude","SWEPT_FACE",FACE,{"disambiguationData":[OSD([sQuery(id+"F14.wireOp",EDGE,"E44")])]}),"instanceName":"3"})});
            var Q7;
            Q7=makeQuery(id+"F16.boolean.opBoolean","COPY",FACE,{"derivedFrom":makeQuery(id+"F16.opPattern","COPY",FACE,{"derivedFrom":makeQuery(id+"F15.opExtrude","SWEPT_FACE",FACE,{"disambiguationData":[OSD([sQuery(id+"F14.wireOp",EDGE,"E44")])]}),"instanceName":"4"})});
            var Q8;
            Q8=makeQuery(id+"F16.boolean.opBoolean","COPY",FACE,{"derivedFrom":makeQuery(id+"F16.opPattern","COPY",FACE,{"derivedFrom":makeQuery(id+"F15.opExtrude","SWEPT_FACE",FACE,{"disambiguationData":[OSD([sQuery(id+"F14.wireOp",EDGE,"E44")])]}),"instanceName":"5"})});
            var Q9;
            Q9=makeQuery(id+"F16.boolean.opBoolean","COPY",FACE,{"derivedFrom":makeQuery(id+"F16.opPattern","COPY",FACE,{"derivedFrom":makeQuery(id+"F15.opExtrude","SWEPT_FACE",FACE,{"disambiguationData":[OSD([sQuery(id+"F14.wireOp",EDGE,"E44")])]}),"instanceName":"6"})});
            var Q10;
            Q10=makeQuery(id+"F16.boolean.opBoolean","COPY",FACE,{"derivedFrom":makeQuery(id+"F16.opPattern","COPY",FACE,{"derivedFrom":makeQuery(id+"F15.opExtrude","SWEPT_FACE",FACE,{"disambiguationData":[OSD([sQuery(id+"F14.wireOp",EDGE,"E44")])]}),"instanceName":"7"})});
            var Q11;
            Q11=makeQuery(id+"F16.boolean.opBoolean","COPY",FACE,{"derivedFrom":makeQuery(id+"F16.opPattern","COPY",FACE,{"derivedFrom":makeQuery(id+"F15.opExtrude","SWEPT_FACE",FACE,{"disambiguationData":[OSD([sQuery(id+"F14.wireOp",EDGE,"E44")])]}),"instanceName":"8"})});
            var Q12;
            Q12=makeQuery(id+"F16.boolean.opBoolean","COPY",FACE,{"derivedFrom":makeQuery(id+"F16.opPattern","COPY",FACE,{"derivedFrom":makeQuery(id+"F15.opExtrude","SWEPT_FACE",FACE,{"disambiguationData":[OSD([sQuery(id+"F14.wireOp",EDGE,"E44")])]}),"instanceName":"9"})});
            var Q13;
            Q13=makeQuery(id+"F16.boolean.opBoolean","COPY",EDGE,{"derivedFrom":makeQuery(id+"F16.opPattern","COPY",EDGE,{"derivedFrom":makeQuery(id+"F15.opExtrude","CAP_EDGE",EDGE,{"disambiguationData":[OSD([sQuery(id+"F14.wireOp",EDGE,"E44")])],"isStart":true}),"instanceName":"10"})});
            var Q14;
            Q14=makeQuery(id+"F16.boolean.opBoolean","COPY",EDGE,{"derivedFrom":makeQuery(id+"F16.opPattern","COPY",EDGE,{"derivedFrom":makeQuery(id+"F15.opExtrude","CAP_EDGE",EDGE,{"disambiguationData":[OSD([sQuery(id+"F14.wireOp",EDGE,"E44")])],"isStart":false}),"instanceName":"10"})});
            var Q15;
            Q15=makeQuery(id+"F16.boolean.opBoolean","COPY",FACE,{"derivedFrom":makeQuery(id+"F16.opPattern","COPY",FACE,{"derivedFrom":makeQuery(id+"F15.opExtrude","SWEPT_FACE",FACE,{"disambiguationData":[OSD([sQuery(id+"F14.wireOp",EDGE,"E44")])]}),"instanceName":"11"})});
            var Q16;
            Q16=makeQuery(id+"F16.boolean.opBoolean","COPY",EDGE,{"derivedFrom":makeQuery(id+"F16.opPattern","COPY",EDGE,{"derivedFrom":makeQuery(id+"F15.opExtrude","CAP_EDGE",EDGE,{"disambiguationData":[OSD([sQuery(id+"F14.wireOp",EDGE,"E44")])],"isStart":true}),"instanceName":"12"})});
            var Q17;
            Q17=makeQuery(id+"F16.boolean.opBoolean","COPY",EDGE,{"derivedFrom":makeQuery(id+"F16.opPattern","COPY",EDGE,{"derivedFrom":makeQuery(id+"F15.opExtrude","CAP_EDGE",EDGE,{"disambiguationData":[OSD([sQuery(id+"F14.wireOp",EDGE,"E44")])],"isStart":false}),"instanceName":"12"})});
            var Q18;
            Q18=makeQuery(id+"F16.boolean.opBoolean","COPY",EDGE,{"derivedFrom":makeQuery(id+"F16.opPattern","COPY",EDGE,{"derivedFrom":makeQuery(id+"F15.opExtrude","CAP_EDGE",EDGE,{"disambiguationData":[OSD([sQuery(id+"F14.wireOp",EDGE,"E44")])],"isStart":true}),"instanceName":"13"})});
            var Q19;
            Q19=makeQuery(id+"F16.boolean.opBoolean","COPY",EDGE,{"derivedFrom":makeQuery(id+"F16.opPattern","COPY",EDGE,{"derivedFrom":makeQuery(id+"F15.opExtrude","CAP_EDGE",EDGE,{"disambiguationData":[OSD([sQuery(id+"F14.wireOp",EDGE,"E44")])],"isStart":false}),"instanceName":"13"})});
            var Q20;
            Q20=makeQuery(id+"F16.boolean.opBoolean","COPY",FACE,{"derivedFrom":makeQuery(id+"F16.opPattern","COPY",FACE,{"derivedFrom":makeQuery(id+"F15.opExtrude","SWEPT_FACE",FACE,{"disambiguationData":[OSD([sQuery(id+"F14.wireOp",EDGE,"E44")])]}),"instanceName":"14"})});
            var Q21;
            Q21=makeQuery(id+"F16.boolean.opBoolean","COPY",FACE,{"derivedFrom":makeQuery(id+"F16.opPattern","COPY",FACE,{"derivedFrom":makeQuery(id+"F15.opExtrude","SWEPT_FACE",FACE,{"disambiguationData":[OSD([sQuery(id+"F14.wireOp",EDGE,"E44")])]}),"instanceName":"15"})});
            var Q22;
            Q22=makeQuery(id+"F16.boolean.opBoolean","COPY",FACE,{"derivedFrom":makeQuery(id+"F16.opPattern","COPY",FACE,{"derivedFrom":makeQuery(id+"F15.opExtrude","SWEPT_FACE",FACE,{"disambiguationData":[OSD([sQuery(id+"F14.wireOp",EDGE,"E44")])]}),"instanceName":"16"})});
            var Q23;
            Q23=makeQuery(id+"F16.boolean.opBoolean","COPY",EDGE,{"derivedFrom":makeQuery(id+"F16.opPattern","COPY",EDGE,{"derivedFrom":makeQuery(id+"F15.opExtrude","CAP_EDGE",EDGE,{"disambiguationData":[OSD([sQuery(id+"F14.wireOp",EDGE,"E44")])],"isStart":false}),"instanceName":"17"})});
            var Q24;
            Q24=makeQuery(id+"F16.boolean.opBoolean","COPY",EDGE,{"derivedFrom":makeQuery(id+"F16.opPattern","COPY",EDGE,{"derivedFrom":makeQuery(id+"F15.opExtrude","CAP_EDGE",EDGE,{"disambiguationData":[OSD([sQuery(id+"F14.wireOp",EDGE,"E44")])],"isStart":true}),"instanceName":"17"})});
            var Q25;
            Q25=makeQuery(id+"F16.boolean.opBoolean","COPY",EDGE,{"derivedFrom":makeQuery(id+"F16.opPattern","COPY",EDGE,{"derivedFrom":makeQuery(id+"F15.opExtrude","CAP_EDGE",EDGE,{"disambiguationData":[OSD([sQuery(id+"F14.wireOp",EDGE,"E44")])],"isStart":false}),"instanceName":"18"})});
            var Q26;
            Q26=makeQuery(id+"F16.boolean.opBoolean","COPY",EDGE,{"derivedFrom":makeQuery(id+"F16.opPattern","COPY",EDGE,{"derivedFrom":makeQuery(id+"F15.opExtrude","CAP_EDGE",EDGE,{"disambiguationData":[OSD([sQuery(id+"F14.wireOp",EDGE,"E44")])],"isStart":true}),"instanceName":"18"})});
            var Q27;
            Q27=makeQuery(id+"F16.boolean.opBoolean","COPY",EDGE,{"derivedFrom":makeQuery(id+"F16.opPattern","COPY",EDGE,{"derivedFrom":makeQuery(id+"F15.opExtrude","CAP_EDGE",EDGE,{"disambiguationData":[OSD([sQuery(id+"F14.wireOp",EDGE,"E44")])],"isStart":false}),"instanceName":"19"})});
            var Q28;
            Q28=makeQuery(id+"F16.boolean.opBoolean","COPY",EDGE,{"derivedFrom":makeQuery(id+"F16.opPattern","COPY",EDGE,{"derivedFrom":makeQuery(id+"F15.opExtrude","CAP_EDGE",EDGE,{"disambiguationData":[OSD([sQuery(id+"F14.wireOp",EDGE,"E44")])],"isStart":true}),"instanceName":"19"})});
            fillet(context, id + "F45", {"entities" : qUnion([Q0, Q1, Q2, Q3, Q4, Q5, Q6, Q7, Q8, Q9, Q10, Q11, Q12, Q13, Q14, Q15, Q16, Q17, Q18, Q19, Q20, Q21, Q22, Q23, Q24, Q25, Q26, Q27, Q28]), "radius" : 1 * mm, "tangentPropagation" : true, "allowEdgeOverflow" : false});
        }
        {
            var Q0;
            Q0=makeQuery(id+"F13.opRevolve","SWEPT_EDGE",EDGE,{"disambiguationData":[OSD([sQuery(id+"F12.wireOp",EDGE,"E41"),sQuery(id+"F12.wireOp",EDGE,"E42")])]});
            var Q1;
            Q1=makeQuery(id+"F13.opRevolve","SWEPT_EDGE",EDGE,{"disambiguationData":[OSD([sQuery(id+"F12.wireOp",EDGE,"E35"),sQuery(id+"F12.wireOp",EDGE,"E42")])]});
            fillet(context, id + "F46", {"entities" : qUnion([Q0, Q1]), "radius" : 1 * mm, "tangentPropagation" : true, "allowEdgeOverflow" : false});
        }
        {
            var Q0;
            Q0=makeQuery(id+"F20.opExtrude","SWEPT_FACE",FACE,{"disambiguationData":[OSD([sQuery(id+"F0.wireOp",EDGE,"E4"),sQuery(id+"F0.wireOp",EDGE,"E5")])]});
            fillet(context, id + "F47", {"entities" : qUnion([Q0]), "radius" : 2 * mm, "tangentPropagation" : true, "allowEdgeOverflow" : false});
        }
        {
            var Q0;
            Q0=makeQuery(id+"F34.opRevolve","SWEPT_FACE",FACE,{"disambiguationData":[OSD([sQuery(id+"F33.wireOp",EDGE,"E67.bottom")])]});
            var Q1;
            Q1=makeQuery(id+"F34.opRevolve","SWEPT_FACE",FACE,{"disambiguationData":[OSD([sQuery(id+"F33.wireOp",EDGE,"E67.top")])]});
            fillet(context, id + "F48", {"entities" : qUnion([Q0, Q1]), "radius" : 2 * mm, "tangentPropagation" : true, "allowEdgeOverflow" : false});
        }
        {
            var Q0;
            Q0=makeQuery(id+"F36.opRevolve","SWEPT_FACE",FACE,{"disambiguationData":[OSD([sQuery(id+"F35.wireOp",EDGE,"E69.right")])]});
            var Q1;
            Q1=makeQuery(id+"F36.opRevolve","SWEPT_FACE",FACE,{"disambiguationData":[OSD([sQuery(id+"F35.wireOp",EDGE,"E69.left")])]});
            fillet(context, id + "F49", {"entities" : qUnion([Q0, Q1]), "radius" : 1 * mm, "tangentPropagation" : true, "allowEdgeOverflow" : false});
        }
    });
